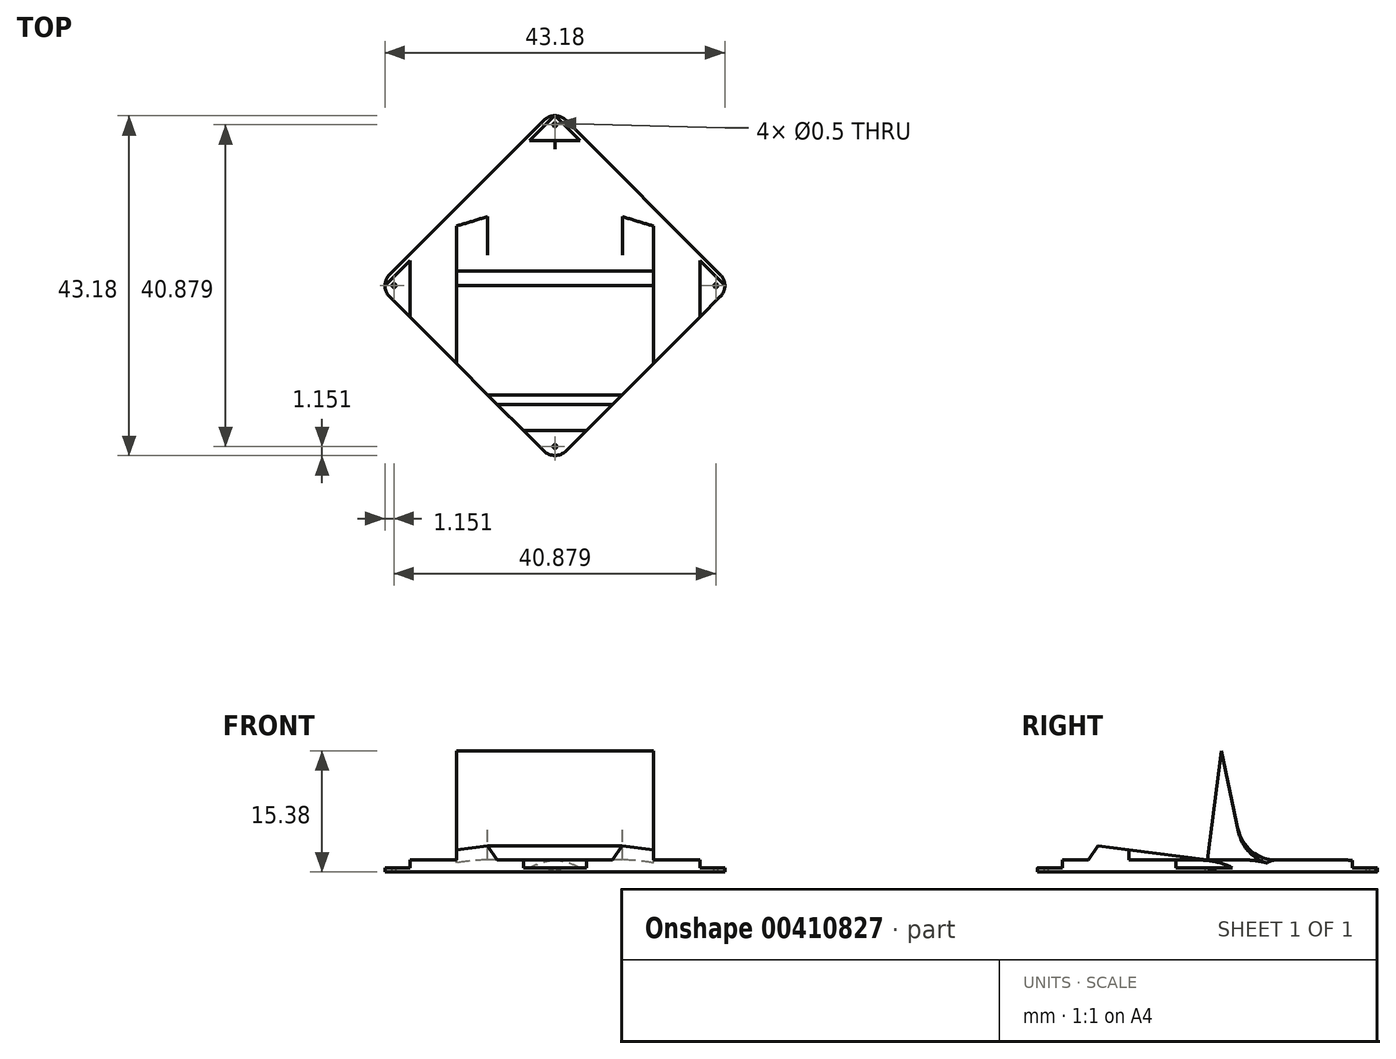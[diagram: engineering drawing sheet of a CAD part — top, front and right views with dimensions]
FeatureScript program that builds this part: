
annotation { "Feature Type Name" : "Feature", "Feature Type Description" : "" }
export const myFeature = defineFeature(function(context is Context, id is Id, definition is map)
    precondition{}
    {
        {
            var Q0;
            Q0=qCreatedBy(makeId("Top.planeOp"),FACE);
            var sketch = newSketch(context, id + "F0", { "sketchPlane" : qUnion([Q0])});
            skLineSegment(sketch, "E0", {"start": v(-21, 1.41) * mm, "end": v(-1.41, 21) * mm});
            skLineSegment(sketch, "E1", {"start": v(1.41, 21) * mm, "end": v(21, 1.41) * mm});
            skLineSegment(sketch, "E2", {"start": v(21, -1.41) * mm, "end": v(1.41, -21) * mm});
            skLineSegment(sketch, "E3", {"start": v(-1.41, -21) * mm, "end": v(-21, -1.41) * mm});
            skPoint(sketch, "E4.visualSharp", {"position": v(0, 22.41) * mm});
            skArc(sketch, "E4.filletArc", {"start": v(1.41, 21) * mm, "mid": v(0, 21.59) * mm, "end": v(-1.41, 21) * mm});
            skPoint(sketch, "E5.visualSharp", {"position": v(0, -22.41) * mm});
            skArc(sketch, "E5.filletArc", {"start": v(-1.41, -21) * mm, "mid": v(0, -21.59) * mm, "end": v(1.41, -21) * mm});
            skPoint(sketch, "E6.visualSharp", {"position": v(22.41, 0) * mm});
            skArc(sketch, "E6.filletArc", {"start": v(21, -1.41) * mm, "mid": v(21.59, 0) * mm, "end": v(21, 1.41) * mm});
            skPoint(sketch, "E7.visualSharp", {"position": v(-22.41, 0) * mm});
            skArc(sketch, "E7.filletArc", {"start": v(-21, 1.41) * mm, "mid": v(-21.59, 0) * mm, "end": v(-21, -1.41) * mm});
            skSolve(sketch);
        }
        {
            var Q0;
            Q0 = qSketchRegion(id + "F0", true);
            extrude(context, id + "F1", {"entities" : qUnion([Q0]), "depth" : 1.5 * mm});
        }
        {
            var Q0;
            Q0=makeQuery(id+"F1.opExtrude","CAP_FACE",FACE,{"disambiguationData":[OSD([sQuery(id+"F0.wireOp",EDGE,"E0"),sQuery(id+"F0.wireOp",EDGE,"E1"),sQuery(id+"F0.wireOp",EDGE,"E2"),sQuery(id+"F0.wireOp",EDGE,"E3")])],"isStart":false});
            var sketch = newSketch(context, id + "F2", { "sketchPlane" : qUnion([Q0])});
            skCircle(sketch, "E8", {"center": v(0, 20.44) * mm, "radius": 0.25 * mm});
            skCircle(sketch, "E9.1.0", {"center": v(-20.44, 0) * mm, "radius": 0.25 * mm});
            skCircle(sketch, "E9.2.0", {"center": v(0, -20.44) * mm, "radius": 0.25 * mm});
            skPoint(sketch, "E9.center", {"position": v(0, 0) * mm});
            skCircle(sketch, "E10.1.3.0", {"center": v(20.44, 0) * mm, "radius": 0.25 * mm});
            skSolve(sketch);
        }
        {
            var Q0;
            Q0 = qSketchRegion(id + "F2", true);
            extrude(context, id + "F3", {"entities" : qUnion([Q0]), "operationType" : NewBodyOperationType.REMOVE, "oppositeDirection" : true, "depth" : 25 * mm});
        }
        {
            var Q0;
            Q0=qCreatedBy(makeId("Right.planeOp"),FACE);
            var sketch = newSketch(context, id + "F4", { "sketchPlane" : qUnion([Q0])});
            skLineSegment(sketch, "E11", {"start": v(0, 1.5) * mm, "end": v(-13.88, 3.33) * mm});
            skLineSegment(sketch, "E12", {"start": v(0, 1.5) * mm, "end": v(1.83, 15.38) * mm});
            skLineSegment(sketch, "E13", {"start": v(1.83, 15.38) * mm, "end": v(4.86, 0.83) * mm});
            skLineSegment(sketch, "E14", {"start": v(-13.88, 3.33) * mm, "end": v(-15.52, 0.83) * mm});
            skLineSegment(sketch, "E15", {"start": v(-15.52, 0.83) * mm, "end": v(4.86, 0.83) * mm});
            skSolve(sketch);
        }
        {
            var Q0;
            Q0 = qSketchRegion(id + "F4", true);
            extrude(context, id + "F5", {"entities" : qUnion([Q0]), "operationType" : NewBodyOperationType.ADD, "depth" : 25 * mm, "symmetric" : true});
        }
        {
            var Q0;
            Q0=makeQuery(id+"F1.opExtrude","CAP_FACE",FACE,{"disambiguationData":[OSD([sQuery(id+"F0.wireOp",EDGE,"E0"),sQuery(id+"F0.wireOp",EDGE,"E1"),sQuery(id+"F0.wireOp",EDGE,"E2"),sQuery(id+"F0.wireOp",EDGE,"E3"),sQuery(id+"F0.wireOp",EDGE,"E4.filletArc"),sQuery(id+"F0.wireOp",EDGE,"E5.filletArc"),sQuery(id+"F0.wireOp",EDGE,"E6.filletArc"),sQuery(id+"F0.wireOp",EDGE,"E7.filletArc")])],"isStart":true});
            var sketch = newSketch(context, id + "F6", { "sketchPlane" : qUnion([Q0])});
            skLineSegment(sketch, "E16", {"start": v(-13.92, 8.5) * mm, "end": v(0, 22.41) * mm});
            skLineSegment(sketch, "E17", {"start": v(0, 22.41) * mm, "end": v(14.29, 8.13) * mm});
            skLineSegment(sketch, "E18", {"start": v(14.29, 8.13) * mm, "end": v(14.29, 30.78) * mm});
            skLineSegment(sketch, "E19", {"start": v(-13.92, 8.5) * mm, "end": v(-13.92, 31) * mm});
            skLineSegment(sketch, "E20", {"start": v(-13.92, 31) * mm, "end": v(14.29, 30.78) * mm});
            skSolve(sketch);
        }
        {
            var Q0;
            Q0 = qSketchRegion(id + "F6", true);
            extrude(context, id + "F7", {"entities" : qUnion([Q0]), "operationType" : NewBodyOperationType.REMOVE, "oppositeDirection" : true, "depth" : 25 * mm});
        }
        {
            var Q0;
            {var subQ0=sQuery(id+"F0.wireOp",EDGE,"E7.filletArc");var subQ1=sQuery(id+"F0.wireOp",EDGE,"E6.filletArc");var subQ2=sQuery(id+"F0.wireOp",EDGE,"E4.filletArc");var subQ3=sQuery(id+"F0.wireOp",EDGE,"E0");var subQ4=sQuery(id+"F0.wireOp",EDGE,"E3");var subQ5=sQuery(id+"F0.wireOp",EDGE,"E1");var subQ6=sQuery(id+"F0.wireOp",EDGE,"E2");Q0=makeQuery(id+"F5.boolean.opBoolean","SPLIT",FACE,{"disambiguationData":[TD([makeQuery(id+"F1.opExtrude","SWEPT_FACE",FACE,{"disambiguationData":[OSD([subQ3])]})])],"derivedFrom":makeQuery(id+"F1.opExtrude","CAP_FACE",FACE,{"disambiguationData":[OSD([subQ3,subQ5,subQ6,subQ4,subQ2,sQuery(id+"F0.wireOp",EDGE,"E5.filletArc"),subQ1,subQ0])],"isStart":false})});}
            var sketch = newSketch(context, id + "F8", { "sketchPlane" : qUnion([Q0])});
            skLineSegment(sketch, "E21.bottom", {"start": v(-5.88, 22.47) * mm, "end": v(5.88, 22.47) * mm});
            skLineSegment(sketch, "E21.top", {"start": v(-5.88, 18.41) * mm, "end": v(5.88, 18.41) * mm});
            skLineSegment(sketch, "E21.left", {"start": v(-5.88, 22.47) * mm, "end": v(-5.88, 18.41) * mm});
            skLineSegment(sketch, "E21.right", {"start": v(5.88, 22.47) * mm, "end": v(5.88, 18.41) * mm});
            skPoint(sketch, "E21.middle", {"position": v(0, 20.44) * mm});
            skLineSegment(sketch, "E22.1.0", {"start": v(-22.47, 5.88) * mm, "end": v(-18.41, 5.88) * mm});
            skLineSegment(sketch, "E22.1.1", {"start": v(-22.47, -5.88) * mm, "end": v(-18.41, -5.88) * mm});
            skLineSegment(sketch, "E22.1.2", {"start": v(-18.41, -5.88) * mm, "end": v(-18.41, 5.88) * mm});
            skLineSegment(sketch, "E22.1.3", {"start": v(-22.47, -5.88) * mm, "end": v(-22.47, 5.88) * mm});
            skLineSegment(sketch, "E22.2.0", {"start": v(-5.88, -22.47) * mm, "end": v(-5.88, -18.41) * mm});
            skLineSegment(sketch, "E22.2.1", {"start": v(5.88, -22.47) * mm, "end": v(5.88, -18.41) * mm});
            skLineSegment(sketch, "E22.2.2", {"start": v(5.88, -18.41) * mm, "end": v(-5.88, -18.41) * mm});
            skLineSegment(sketch, "E22.2.3", {"start": v(5.88, -22.47) * mm, "end": v(-5.88, -22.47) * mm});
            skLineSegment(sketch, "E22.3.0", {"start": v(22.47, -5.88) * mm, "end": v(18.41, -5.88) * mm});
            skLineSegment(sketch, "E22.3.1", {"start": v(22.47, 5.88) * mm, "end": v(18.41, 5.88) * mm});
            skLineSegment(sketch, "E22.3.2", {"start": v(18.41, 5.88) * mm, "end": v(18.41, -5.88) * mm});
            skLineSegment(sketch, "E22.3.3", {"start": v(22.47, 5.88) * mm, "end": v(22.47, -5.88) * mm});
            skPoint(sketch, "E22.center", {"position": v(0, 0) * mm});
            skSolve(sketch);
        }
        {
            var Q0;
            Q0 = qSketchRegion(id + "F8", true);
            extrude(context, id + "F9", {"entities" : qUnion([Q0]), "operationType" : NewBodyOperationType.REMOVE, "oppositeDirection" : true, "depth" : 1 * mm});
        }
        {
            var Q0;
            Q0=makeQuery(id+"F1.opExtrude","CAP_EDGE",EDGE,{"disambiguationData":[OSD([sQuery(id+"F0.wireOp",EDGE,"E1")])],"isStart":false});
            var Q1;
            Q1=makeQuery(id+"F1.opExtrude","CAP_EDGE",EDGE,{"disambiguationData":[OSD([sQuery(id+"F0.wireOp",EDGE,"E0")])],"isStart":false});
            var Q2;
            {var subQ0=sQuery(id+"F0.wireOp",EDGE,"E6.filletArc");var subQ1=sQuery(id+"F0.wireOp",EDGE,"E2");Q2=makeQuery(id+"F5.boolean.opBoolean","SPLIT",EDGE,{"disambiguationData":[TD([makeQuery(id+"F1.opExtrude","SWEPT_FACE",FACE,{"disambiguationData":[OSD([subQ0])]})])],"derivedFrom":makeQuery(id+"F1.opExtrude","CAP_EDGE",EDGE,{"disambiguationData":[OSD([subQ1])],"isStart":false})});}
            var Q3;
            {var subQ0=sQuery(id+"F0.wireOp",EDGE,"E7.filletArc");var subQ1=sQuery(id+"F0.wireOp",EDGE,"E3");Q3=makeQuery(id+"F5.boolean.opBoolean","SPLIT",EDGE,{"disambiguationData":[TD([makeQuery(id+"F1.opExtrude","SWEPT_FACE",FACE,{"disambiguationData":[OSD([subQ0])]})])],"derivedFrom":makeQuery(id+"F1.opExtrude","CAP_EDGE",EDGE,{"disambiguationData":[OSD([subQ1])],"isStart":false})});}
            var Q4;
            {var subQ0=sQuery(id+"F0.wireOp",EDGE,"E5.filletArc");var subQ1=sQuery(id+"F0.wireOp",EDGE,"E3");Q4=makeQuery(id+"F5.boolean.opBoolean","SPLIT",EDGE,{"disambiguationData":[TD([makeQuery(id+"F1.opExtrude","SWEPT_FACE",FACE,{"disambiguationData":[OSD([subQ0])]})])],"derivedFrom":makeQuery(id+"F1.opExtrude","CAP_EDGE",EDGE,{"disambiguationData":[OSD([subQ1])],"isStart":false})});}
            var Q5;
            {var subQ0=sQuery(id+"F0.wireOp",EDGE,"E5.filletArc");var subQ1=sQuery(id+"F0.wireOp",EDGE,"E2");Q5=makeQuery(id+"F5.boolean.opBoolean","SPLIT",EDGE,{"disambiguationData":[TD([makeQuery(id+"F1.opExtrude","SWEPT_FACE",FACE,{"disambiguationData":[OSD([subQ0])]})])],"derivedFrom":makeQuery(id+"F1.opExtrude","CAP_EDGE",EDGE,{"disambiguationData":[OSD([subQ1])],"isStart":false})});}
            fillet(context, id + "F10", {"entities" : qUnion([Q0, Q1, Q2, Q3, Q4, Q5]), "radius" : 5 * mm, "tangentPropagation" : true, "allowEdgeOverflow" : false});
        }
        {
            var Q0;
            Q0=makeQuery(id+"F5.boolean.opBoolean","INTERSECT",EDGE,{"derivedFrom":[makeQuery(id+"F1.opExtrude","CAP_FACE",FACE,{"disambiguationData":[OSD([sQuery(id+"F0.wireOp",EDGE,"E0"),sQuery(id+"F0.wireOp",EDGE,"E1"),sQuery(id+"F0.wireOp",EDGE,"E2"),sQuery(id+"F0.wireOp",EDGE,"E3"),sQuery(id+"F0.wireOp",EDGE,"E4.filletArc"),sQuery(id+"F0.wireOp",EDGE,"E5.filletArc"),sQuery(id+"F0.wireOp",EDGE,"E6.filletArc"),sQuery(id+"F0.wireOp",EDGE,"E7.filletArc")])],"isStart":false}),makeQuery(id+"F5.opExtrude","SWEPT_FACE",FACE,{"disambiguationData":[OSD([sQuery(id+"F4.wireOp",EDGE,"E13")])]})]});
            fillet(context, id + "F11", {"entities" : qUnion([Q0]), "radius" : 5 * mm, "tangentPropagation" : true, "allowEdgeOverflow" : false});
        }
    });
